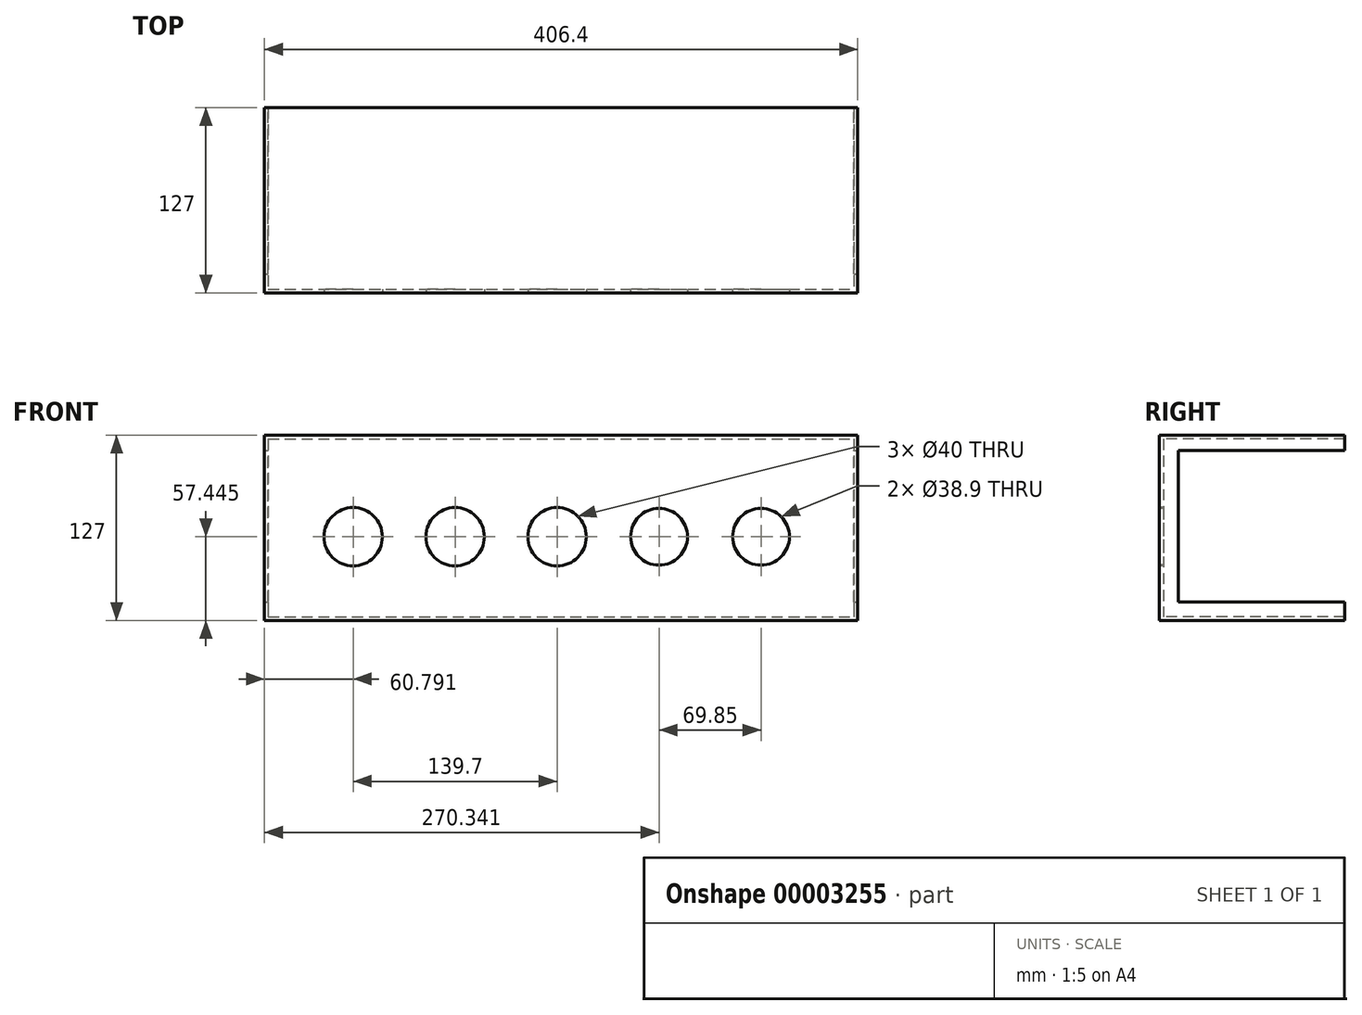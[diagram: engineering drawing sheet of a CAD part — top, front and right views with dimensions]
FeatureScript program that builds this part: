
annotation { "Feature Type Name" : "Feature", "Feature Type Description" : "" }
export const myFeature = defineFeature(function(context is Context, id is Id, definition is map)
    precondition{}
    {
        {
            var Q0;
            Q0=qCreatedBy(makeId("Top.planeOp"),FACE);
            var sketch = newSketch(context, id + "F0", { "sketchPlane" : qUnion([Q0])});
            skLineSegment(sketch, "E0.bottom", {"start": v(-203.2, 127) * mm, "end": v(203.2, 127) * mm});
            skLineSegment(sketch, "E0.top", {"start": v(-203.2, 0) * mm, "end": v(203.2, 0) * mm});
            skLineSegment(sketch, "E0.left", {"start": v(-203.2, 127) * mm, "end": v(-203.2, 0) * mm});
            skLineSegment(sketch, "E0.right", {"start": v(203.2, 127) * mm, "end": v(203.2, 0) * mm});
            skLineSegment(sketch, "E1", {"start": v(0, 0) * mm, "end": v(0, 16.27) * mm});
            skSolve(sketch);
        }
        {
            var Q0;
            Q0=makeQuery(id+"F0.imprint","IMPRINT",FACE,{"disambiguationData":[TD([[makeQuery(id+"F0.imprint","IMPRINT",EDGE,{"derivedFrom":sQuery(id+"F0.wireOp",EDGE,"E0.bottom")}),-1.0]])]});
            extrude(context, id + "F1", {"entities" : qUnion([Q0]), "depth" : 127 * mm});
        }
        {
            var Q0;
            Q0=makeQuery(id+"F1.opExtrude","SWEPT_FACE",FACE,{"disambiguationData":[OSD([sQuery(id+"F0.wireOp",EDGE,"E0.bottom")])]});
            shell(context, id + "F2", {"entities" : qUnion([Q0]), "thickness" : 2.54 * mm});
        }
        {
            var Q0;
            Q0=makeQuery(id+"F1.opExtrude","SWEPT_FACE",FACE,{"disambiguationData":[OSD([sQuery(id+"F0.wireOp",EDGE,"E0.top")])]});
            var sketch = newSketch(context, id + "F3", { "sketchPlane" : qUnion([Q0])});
            skCircle(sketch, "E2", {"center": v(-2.7, 57.45) * mm, "radius": 20 * mm});
            skCircle(sketch, "E3", {"center": v(137, 57.45) * mm, "radius": 19.45 * mm});
            skCircle(sketch, "E4", {"center": v(67.14, 57.45) * mm, "radius": 19.45 * mm});
            skCircle(sketch, "E5", {"center": v(-72.56, 57.45) * mm, "radius": 20 * mm});
            skCircle(sketch, "E6", {"center": v(-142.4, 57.45) * mm, "radius": 20 * mm});
            skLineSegment(sketch, "E7", {"start": v(0, 0) * mm, "end": v(0, 17.9) * mm});
            skLineSegment(sketch, "E8", {"start": v(-142.4, 57.45) * mm, "end": v(-72.56, 57.45) * mm});
            skLineSegment(sketch, "E9", {"start": v(-72.56, 57.45) * mm, "end": v(-2.7, 57.45) * mm});
            skLineSegment(sketch, "E10", {"start": v(67.14, 57.45) * mm, "end": v(-2.7, 57.45) * mm});
            skLineSegment(sketch, "E11", {"start": v(137, 57.45) * mm, "end": v(67.14, 57.45) * mm});
            skSolve(sketch);
        }
        {
            var Q0;
            Q0 = qSketchRegion(id + "F3", true);
            extrude(context, id + "F4", {"entities" : qUnion([Q0]), "operationType" : NewBodyOperationType.REMOVE, "endBound" : BoundingType.UP_TO_NEXT, "oppositeDirection" : true, "depth" : 25.4 * mm});
        }
        {
            var Q0;
            Q0=makeQuery(id+"F1.opExtrude","SWEPT_FACE",FACE,{"disambiguationData":[OSD([sQuery(id+"F0.wireOp",EDGE,"E0.right")])]});
            var sketch = newSketch(context, id + "F5", { "sketchPlane" : qUnion([Q0])});
            skLineSegment(sketch, "E12.bottom", {"start": v(12.95, 12.6) * mm, "end": v(127, 12.6) * mm});
            skLineSegment(sketch, "E12.top", {"start": v(12.95, 116.69) * mm, "end": v(127, 116.69) * mm});
            skLineSegment(sketch, "E12.left", {"start": v(12.95, 12.6) * mm, "end": v(12.95, 116.69) * mm});
            skLineSegment(sketch, "E12.right", {"start": v(127, 12.6) * mm, "end": v(127, 116.69) * mm});
            skSolve(sketch);
        }
        {
            var Q0;
            Q0=makeQuery(id+"F5.imprint","IMPRINT",FACE,{"disambiguationData":[TD([[makeQuery(id+"F5.imprint","IMPRINT",EDGE,{"derivedFrom":sQuery(id+"F5.wireOp",EDGE,"E12.bottom")}),1.0]])]});
            extrude(context, id + "F6", {"entities" : qUnion([Q0]), "operationType" : NewBodyOperationType.REMOVE, "endBound" : BoundingType.THROUGH_ALL, "oppositeDirection" : true, "depth" : 25.4 * mm});
        }
    });
